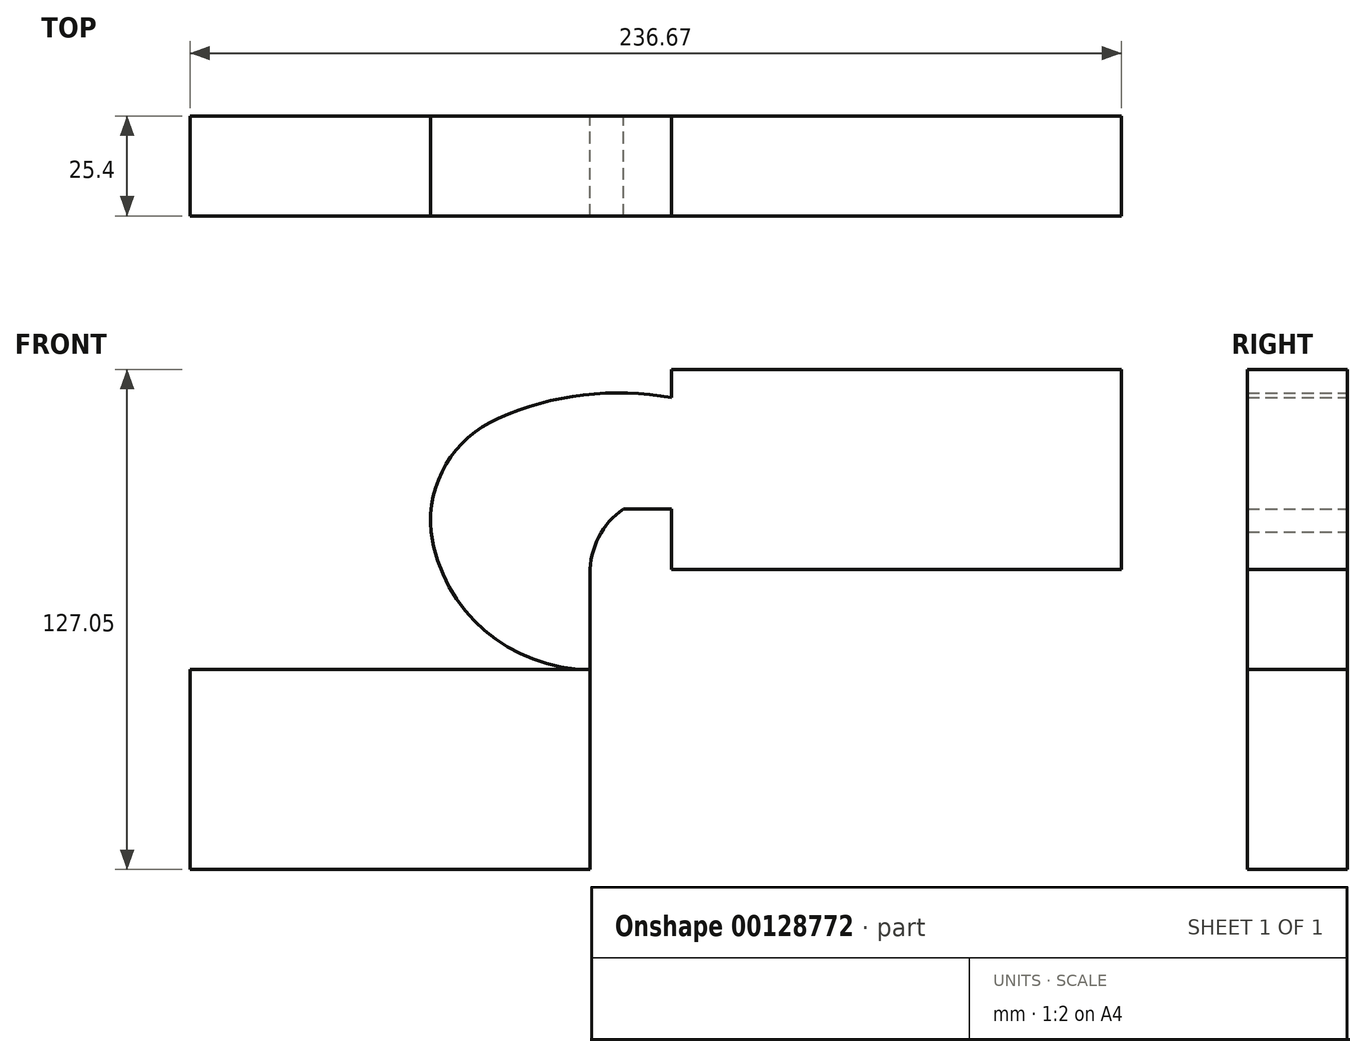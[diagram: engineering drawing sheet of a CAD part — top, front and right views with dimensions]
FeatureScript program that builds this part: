
annotation { "Feature Type Name" : "Feature", "Feature Type Description" : "" }
export const myFeature = defineFeature(function(context is Context, id is Id, definition is map)
    precondition{}
    {
        {
            var Q0;
            Q0=qCreatedBy(makeId("Front.planeOp"),FACE);
            var sketch = newSketch(context, id + "F0", { "sketchPlane" : qUnion([Q0])});
            skLineSegment(sketch, "E0.bottom", {"start": v(-50.8, 25.4) * mm, "end": v(50.8, 25.4) * mm});
            skLineSegment(sketch, "E0.top", {"start": v(-50.8, -25.4) * mm, "end": v(50.8, -25.4) * mm});
            skLineSegment(sketch, "E0.left", {"start": v(-50.8, 25.4) * mm, "end": v(-50.8, -25.4) * mm});
            skLineSegment(sketch, "E0.right", {"start": v(50.8, 25.4) * mm, "end": v(50.8, -25.4) * mm});
            skPoint(sketch, "E0.middle", {"position": v(0, 0) * mm});
            skLineSegment(sketch, "E1", {"start": v(50.8, 25.4) * mm, "end": v(50.8, 38.03) * mm});
            skLineSegment(sketch, "E2", {"start": v(50.8, 38.03) * mm, "end": v(50.8, 49.72) * mm});
            skArc(sketch, "E3", {"start": v(50.8, 49.72) * mm, "mid": v(53.05, 59) * mm, "end": v(59.3, 66.23) * mm});
            skLineSegment(sketch, "E4.top", {"start": v(117.97, 66.23) * mm, "end": v(59.3, 66.23) * mm});
            skLineSegment(sketch, "E5.bottom", {"start": v(71.57, 50.85) * mm, "end": v(185.87, 50.85) * mm});
            skLineSegment(sketch, "E5.top", {"start": v(71.57, 101.65) * mm, "end": v(185.87, 101.65) * mm});
            skLineSegment(sketch, "E5.left", {"start": v(71.57, 50.85) * mm, "end": v(71.57, 101.65) * mm});
            skLineSegment(sketch, "E5.right", {"start": v(185.87, 50.85) * mm, "end": v(185.87, 101.65) * mm});
            skPoint(sketch, "E5.middle", {"position": v(128.72, 76.25) * mm});
            skArc(sketch, "E6", {"start": v(10.4, 60.37) * mm, "mid": v(24.08, 35.36) * mm, "end": v(50.8, 25.4) * mm});
            skArc(sketch, "E7", {"start": v(117.97, 66.23) * mm, "mid": v(76.7, 93.38) * mm, "end": v(27.5, 89.23) * mm});
            skArc(sketch, "E8", {"start": v(27.5, 89.23) * mm, "mid": v(14.26, 77.57) * mm, "end": v(10.4, 60.37) * mm});
            skSolve(sketch);
        }
        {
            var Q0;
            Q0 = qSketchRegion(id + "F0", true);
            extrude(context, id + "F1", {"entities" : qUnion([Q0]), "depth" : 25.4 * mm});
        }
    });
